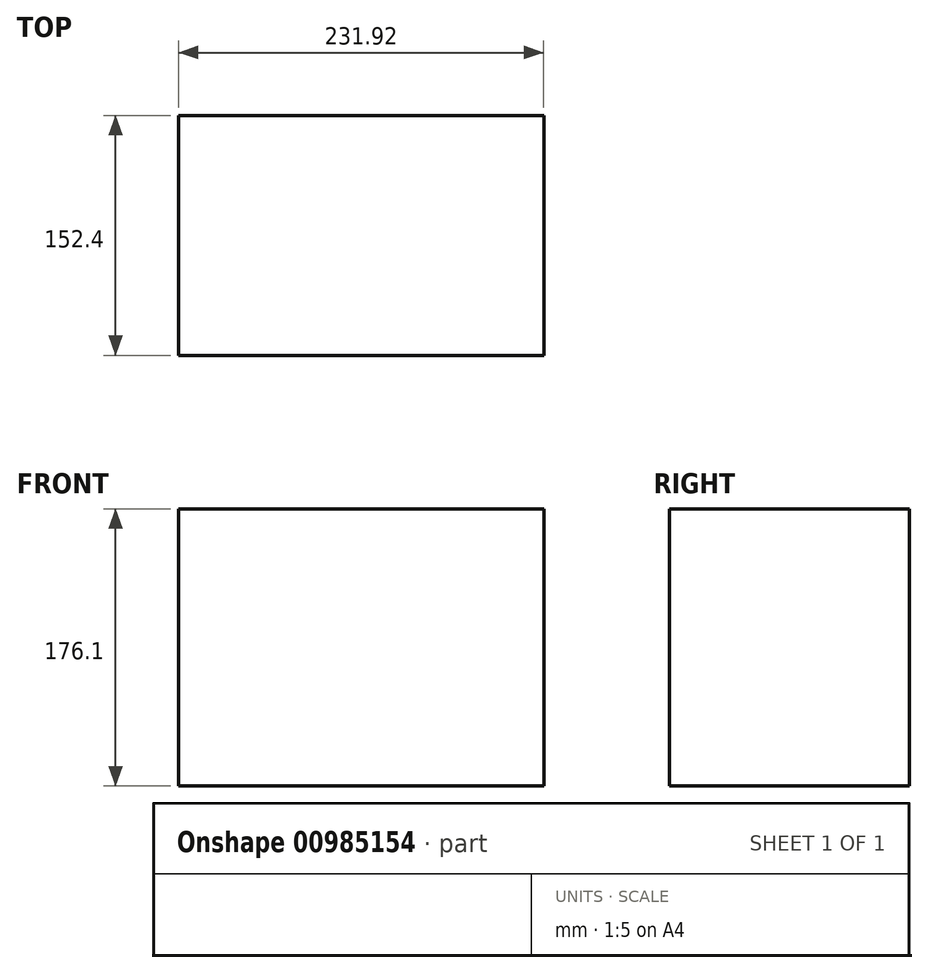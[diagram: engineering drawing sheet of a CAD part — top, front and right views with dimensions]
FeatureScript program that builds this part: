
annotation { "Feature Type Name" : "Feature", "Feature Type Description" : "" }
export const myFeature = defineFeature(function(context is Context, id is Id, definition is map)
    precondition{}
    {
        {
            var Q0;
            Q0=qCreatedBy(makeId("Front.planeOp"),FACE);
            var sketch = newSketch(context, id + "F0", { "sketchPlane" : qUnion([Q0])});
            skLineSegment(sketch, "E0.bottom", {"start": v(-59.63, 49.52) * mm, "end": v(172.3, 49.52) * mm});
            skLineSegment(sketch, "E0.top", {"start": v(-59.63, -126.58) * mm, "end": v(172.3, -126.58) * mm});
            skLineSegment(sketch, "E0.left", {"start": v(-59.63, 49.52) * mm, "end": v(-59.63, -126.58) * mm});
            skLineSegment(sketch, "E0.right", {"start": v(172.3, 49.52) * mm, "end": v(172.3, -126.58) * mm});
            skSolve(sketch);
        }
        {
            var Q0;
            Q0=makeQuery(id+"F0.imprint","IMPRINT",FACE,{"disambiguationData":[TD([[makeQuery(id+"F0.imprint","IMPRINT",EDGE,{"derivedFrom":sQuery(id+"F0.wireOp",EDGE,"E0.bottom")}),-1.0]])]});
            extrude(context, id + "F1", {"entities" : qUnion([Q0]), "depth" : 152.4 * mm, "offsetDistance" : 25.4 * mm});
        }
        {
            var Q0;
            Q0=makeQuery(id+"F1.opExtrude","CAP_FACE",FACE,{"disambiguationData":[OSD([sQuery(id+"F0.wireOp",EDGE,"E0.bottom"),sQuery(id+"F0.wireOp",EDGE,"E0.top"),sQuery(id+"F0.wireOp",EDGE,"E0.left"),sQuery(id+"F0.wireOp",EDGE,"E0.right")])],"isStart":false});
            var sketch = newSketch(context, id + "F2", { "sketchPlane" : qUnion([Q0])});
            skLineSegment(sketch, "E1.bottom", {"start": v(0, 0) * mm, "end": v(140.72, 0) * mm});
            skLineSegment(sketch, "E1.top", {"start": v(0, -8.77) * mm, "end": v(140.72, -8.77) * mm});
            skLineSegment(sketch, "E1.left", {"start": v(0, 0) * mm, "end": v(0, -8.77) * mm});
            skLineSegment(sketch, "E1.right", {"start": v(140.72, 0) * mm, "end": v(140.72, -8.77) * mm});
            skLineSegment(sketch, "E2.bottom", {"start": v(25.2, -33.68) * mm, "end": v(106.37, -33.68) * mm});
            skLineSegment(sketch, "E2.top", {"start": v(25.2, -25.75) * mm, "end": v(106.37, -25.75) * mm});
            skLineSegment(sketch, "E2.left", {"start": v(25.2, -33.68) * mm, "end": v(25.2, -25.75) * mm});
            skLineSegment(sketch, "E2.right", {"start": v(106.37, -33.68) * mm, "end": v(106.37, -25.75) * mm});
            skSolve(sketch);
        }
        {
            var Q0;
            Q0=makeQuery(id+"F2.imprint","IMPRINT",FACE,{"disambiguationData":[TD([[makeQuery(id+"F2.imprint","IMPRINT",EDGE,{"derivedFrom":sQuery(id+"F2.wireOp",EDGE,"E1.bottom")}),-1.0]])]});
            extrude(context, id + "F3", {"entities" : qUnion([Q0]), "operationType" : NewBodyOperationType.ADD, "depth" : -12.7 * mm, "offsetDistance" : 25.4 * mm});
        }
    });
